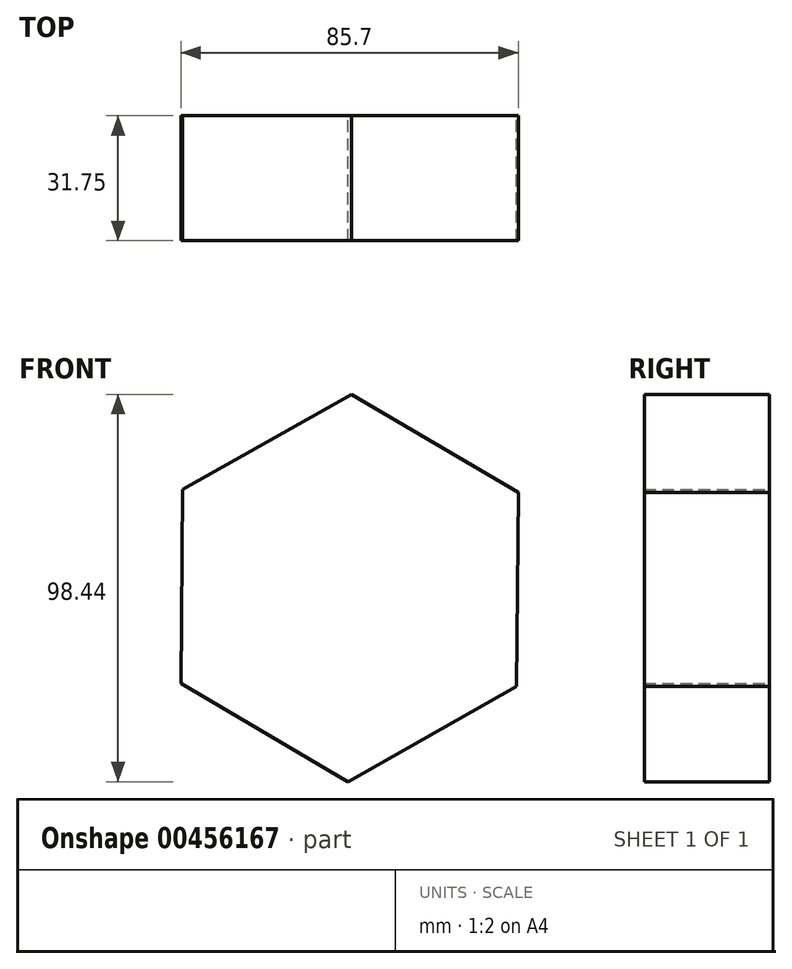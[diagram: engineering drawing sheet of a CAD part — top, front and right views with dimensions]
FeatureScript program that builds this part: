
annotation { "Feature Type Name" : "Feature", "Feature Type Description" : "" }
export const myFeature = defineFeature(function(context is Context, id is Id, definition is map)
    precondition{}
    {
        {
            var Q0;
            Q0=qCreatedBy(makeId("Front.planeOp"),FACE);
            var sketch = newSketch(context, id + "F0", { "sketchPlane" : qUnion([Q0])});
            skCircle(sketch, "E0.cCircle", {"center": v(0, 0) * mm, "radius": 42.63 * mm, "construction": true});
            skLineSegment(sketch, "E0.0", {"start": v(0.44, 49.22) * mm, "end": v(42.85, 24.23) * mm});
            skLineSegment(sketch, "E0.1", {"start": v(42.85, 24.23) * mm, "end": v(42.41, -24.99) * mm});
            skLineSegment(sketch, "E0.2", {"start": v(42.41, -24.99) * mm, "end": v(-0.44, -49.22) * mm});
            skLineSegment(sketch, "E0.3", {"start": v(-0.44, -49.22) * mm, "end": v(-42.85, -24.23) * mm});
            skLineSegment(sketch, "E0.4", {"start": v(-42.85, -24.23) * mm, "end": v(-42.41, 24.99) * mm});
            skLineSegment(sketch, "E0.5", {"start": v(-42.41, 24.99) * mm, "end": v(0.44, 49.22) * mm});
            skPoint(sketch, "E0.0.midPoint", {"position": v(21.64, 36.73) * mm});
            skSolve(sketch);
        }
        {
            var Q0;
            Q0 = qSketchRegion(id + "F0", true);
            extrude(context, id + "F1", {"entities" : qUnion([Q0]), "depth" : 31.75 * mm});
        }
    });
